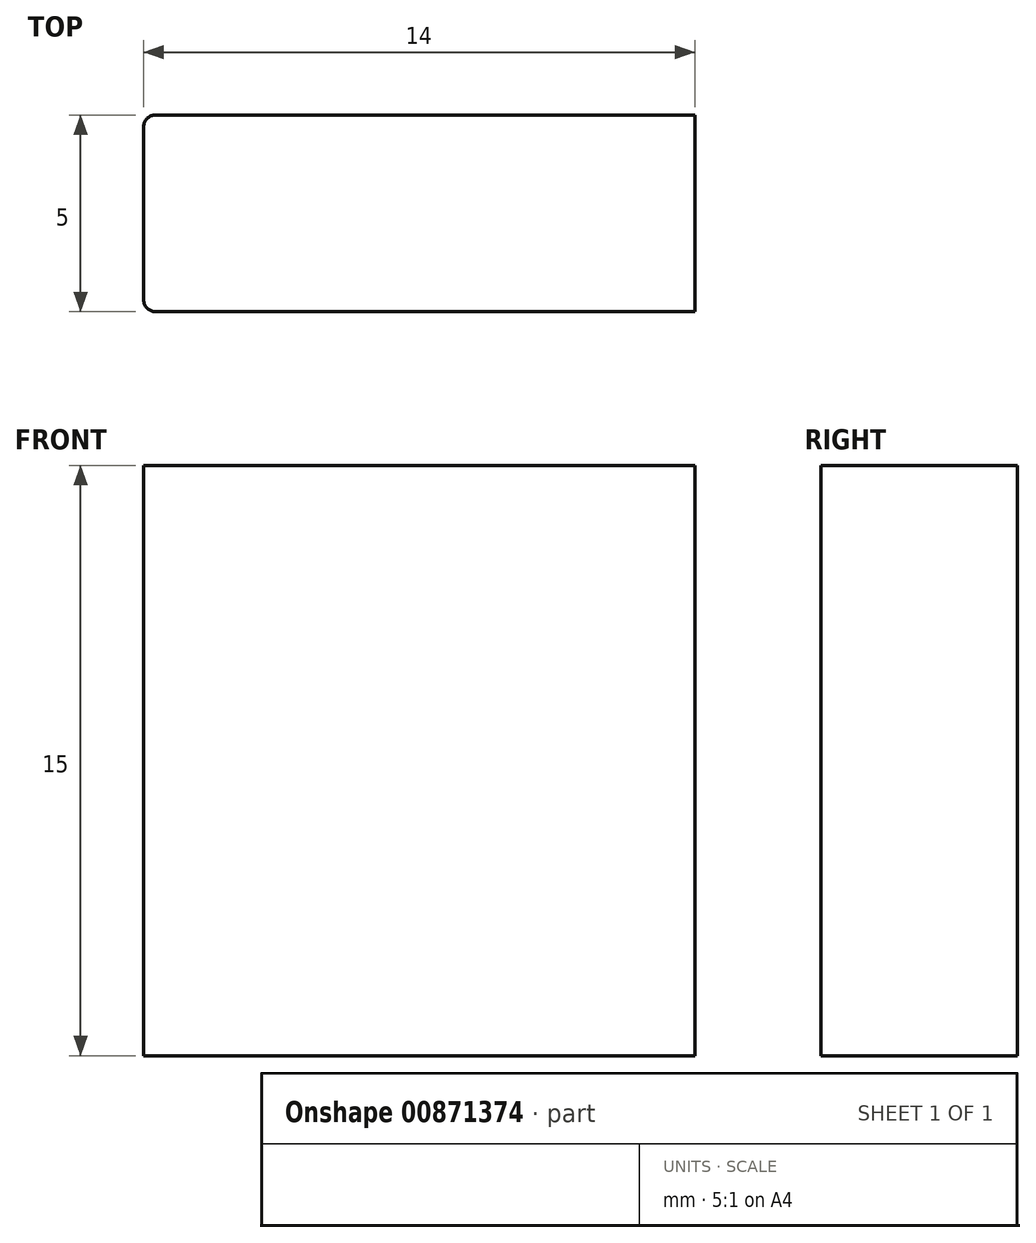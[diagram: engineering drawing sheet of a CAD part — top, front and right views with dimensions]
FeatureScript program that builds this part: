
annotation { "Feature Type Name" : "Feature", "Feature Type Description" : "" }
export const myFeature = defineFeature(function(context is Context, id is Id, definition is map)
    precondition{}
    {
        {
            var Q0;
            Q0=qCreatedBy(makeId("Top.planeOp"),FACE);
            var sketch = newSketch(context, id + "F0", { "sketchPlane" : qUnion([Q0])});
            skLineSegment(sketch, "E0.bottom", {"start": v(-0.67, -4.82) * mm, "end": v(13.03, -4.82) * mm});
            skLineSegment(sketch, "E0.top", {"start": v(-0.67, -9.82) * mm, "end": v(13.03, -9.82) * mm});
            skLineSegment(sketch, "E0.left", {"start": v(-0.97, -5.12) * mm, "end": v(-0.97, -9.52) * mm});
            skLineSegment(sketch, "E0.right", {"start": v(13.03, -4.82) * mm, "end": v(13.03, -9.82) * mm});
            skPoint(sketch, "E1.visualSharp", {"position": v(-0.97, -9.82) * mm});
            skArc(sketch, "E1.filletArc", {"start": v(-0.97, -9.52) * mm, "mid": v(-0.88, -9.73) * mm, "end": v(-0.67, -9.82) * mm});
            skPoint(sketch, "E2.visualSharp", {"position": v(-0.97, -4.82) * mm});
            skArc(sketch, "E2.filletArc", {"start": v(-0.67, -4.82) * mm, "mid": v(-0.88, -4.9) * mm, "end": v(-0.97, -5.12) * mm});
            skSolve(sketch);
        }
        {
            var Q0;
            Q0=qSketchRegion(id+"F0",true);
            extrude(context, id + "F1", {"entities" : qUnion([Q0]), "depth" : 15 * mm, "offsetDistance" : 25 * mm});
        }
    });
